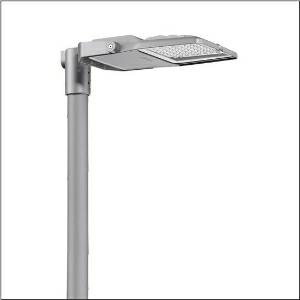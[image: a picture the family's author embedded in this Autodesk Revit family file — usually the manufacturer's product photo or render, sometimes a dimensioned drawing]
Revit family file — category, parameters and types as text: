
# Revit family: floodlight_fl_21_mini___pl64_5xa7776b2e3a_216f
name_source: partatom
category: Lighting Fixtures
units: mm (PartAtom-declared; Revit-internal decimal feet)

## family parameters
Cut with Voids When Loaded = No
Host = Face
Light Source = No
Part Type = Normal
Room Calculation Point = No
Round Connector Dimension = Use Diameter
Shared = No

## types (1)
- --- (1 x LED, 6010 lm, 45.7 W, 3000K)
    Apparent Load = 46 VA
    CIE Flux Codes = 28 80 98 100 100
    Color Rendering = 70
    Color Temperature = 3000K
    Default Elevation = 1800 mm
    Description = Floodlight FL 21 mini, floodlight, primary light control with lens, of PMMA, primary optical cover: protective disc, of toughened safety glass, transparent, light distribution: PL64, light emission: direct distribution, installation type: surface-mounted, LED, High Power LED, rated luminous flux: 6.010lm, luminous efficacy: 132lm/W, light colour: 730, colour temperature: 3000K, control gear: Smart Interface (Zhaga), control: flexible luminous flux parameterisation, time-dependent luminous flux control, constant luminous flux control, overheat protection, pre-setting: logarithmic dimming characteristic, with terminal, 6-pole, mains connection: 220..240V, AC, 50/60Hz, start of lifetime: 46W, end of service life: 48W, reduction: 22W, luminaire housing, of diecast aluminium, powder-coated, SITECO metallic grey (DB 702S), corrosivity category C5 mid according to DIN EN ISO 12944, suitable for swimming pools, chlorine-resistant, sealing non-destructively replaceable, please order mast flange separately, mast bracket, of steel, galvanised, powder-coated, SITECO metallic grey (DB 702S), Smart Interface below and above, protection rating (complete): IP66, insulation class (complete): insulation class II (safety insulation), certification: CE, ENEC, VDE, protection symbol: D, impact resistance: IK08, permissible operating ambient temperature: -40..+40°C, permissible operating ambient temperature for outdoor applications: -40..+50°C, standard: DIN EN 12944, LABS conformity tested according to VDMA 24364:2018-05, packaging unit: 1 piece

Light Distribution: PL64
    Height = 70 mm
    Lamp = 1 x LED
    Lamp Light Flux = 6010 lm
    Lamp Power = 45.7 W
    Lamp count = 1
    Length = 485 mm
    Luminous efficacy = 132 lm/W
    Manufacturer = Siteco
    ModVariant = No
    Model = 5XA7776B2E3A
    Number of Poles = 1
    OnlyDefault = Yes
    Power Factor = 1
    Product Name = Floodlight FL 21 mini | PL64
    Product group = floodlight | pylon annexe
    ProductGroupID = 6201
    Protection Class = Protection class II
    Protection Degree = IP 66
    RLX_Detail_Level = 1
    RLX_Emergency_Light_Flux = 0 lm
    RLX_Emergency_Type = 0
    RLX_Emergency_Type_DB = No
    RlxData = <blob elided: 101225 chars, md5=4b08b789>
    Socket = socket
    Standby Power = 0 W
    System Light Flux = 6010 lm
    System Power = 46 W
    Type Comments = factory setting: luminous flux: 100 % | dim-lin: 254 | 463 mA
    Type Image = l_1007125.jpg
    URL = http://relux.com
    VarID = @adj_164953
    Voltage = 0 V
    Weight = 0.00 kg
    Width = 337 mm

## geometry (parser evidence)
native form markers: Blend x4, Sweep x13
no freeform markers — native parametric forms only
